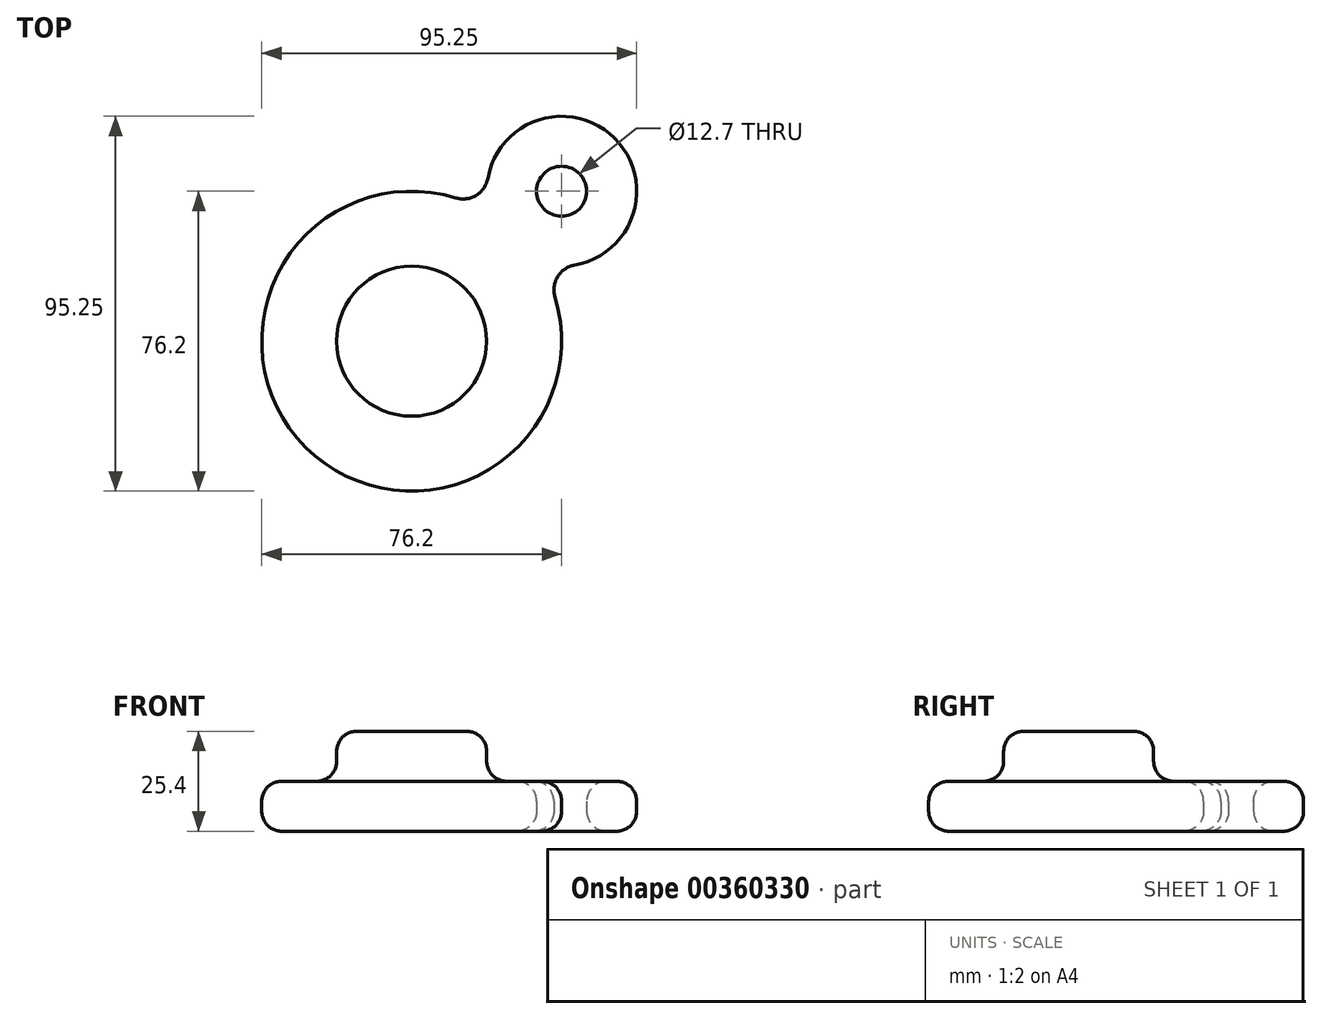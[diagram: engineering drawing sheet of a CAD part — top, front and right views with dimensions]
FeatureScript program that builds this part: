
annotation { "Feature Type Name" : "Feature", "Feature Type Description" : "" }
export const myFeature = defineFeature(function(context is Context, id is Id, definition is map)
    precondition{}
    {
        {
            var Q0;
            Q0=qCreatedBy(makeId("Top.planeOp"),FACE);
            var sketch = newSketch(context, id + "F0", { "sketchPlane" : qUnion([Q0])});
            skArc(sketch, "E0", {"start": v(11.21, 36.41) * mm, "mid": v(-26.94, -26.94) * mm, "end": v(36.41, 11.21) * mm});
            skArc(sketch, "E1", {"start": v(41.39, 19.34) * mm, "mid": v(51.57, 51.57) * mm, "end": v(19.34, 41.39) * mm});
            skPoint(sketch, "E2.visualSharp", {"position": v(19.9, 32.5) * mm});
            skArc(sketch, "E2.filletArc", {"start": v(11.21, 36.41) * mm, "mid": v(16.4, 37.07) * mm, "end": v(19.34, 41.39) * mm});
            skPoint(sketch, "E3.visualSharp", {"position": v(32.5, 19.9) * mm});
            skArc(sketch, "E3.filletArc", {"start": v(41.39, 19.34) * mm, "mid": v(37.07, 16.4) * mm, "end": v(36.41, 11.21) * mm});
            skCircle(sketch, "E4", {"center": v(38.1, 38.1) * mm, "radius": 6.35 * mm});
            skSolve(sketch);
        }
        {
            var Q0;
            Q0=qCreatedBy(makeId("Top.planeOp"),FACE);
            var sketch = newSketch(context, id + "F1", { "sketchPlane" : qUnion([Q0])});
            skCircle(sketch, "E5", {"center": v(0, 0) * mm, "radius": 19.05 * mm});
            skSolve(sketch);
        }
        {
            var Q0;
            Q0=makeQuery(id+"F0.imprint","IMPRINT",FACE,{"disambiguationData":[TD([[makeQuery(id+"F0.imprint","IMPRINT",EDGE,{"derivedFrom":sQuery(id+"F0.wireOp",EDGE,"E0")}),1.0]])]});
            extrude(context, id + "F2", {"entities" : qUnion([Q0]), "depth" : 12.7 * mm});
        }
        {
            var Q0;
            Q0=makeQuery(id+"F1.imprint","IMPRINT",FACE,{"disambiguationData":[TD([[makeQuery(id+"F1.imprint","IMPRINT",EDGE,{"derivedFrom":sQuery(id+"F1.wireOp",EDGE,"E5")}),1.0]])]});
            extrude(context, id + "F3", {"entities" : qUnion([Q0]), "operationType" : NewBodyOperationType.ADD, "depth" : 25.4 * mm});
        }
        {
            var Q0;
            Q0=makeQuery(id+"F3.opExtrude","CAP_EDGE",EDGE,{"disambiguationData":[OSD([sQuery(id+"F1.wireOp",EDGE,"E5")])],"isStart":false});
            var Q1;
            Q1=makeQuery(id+"F2.opExtrude","CAP_EDGE",EDGE,{"disambiguationData":[OSD([sQuery(id+"F0.wireOp",EDGE,"E0")])],"isStart":false});
            var Q2;
            Q2=makeQuery(id+"F2.opExtrude","CAP_EDGE",EDGE,{"disambiguationData":[OSD([sQuery(id+"F0.wireOp",EDGE,"E0")])],"isStart":true});
            var Q3;
            Q3=makeQuery(id+"F3.boolean.opBoolean","INTERSECT",EDGE,{"derivedFrom":[makeQuery(id+"F2.opExtrude","CAP_FACE",FACE,{"disambiguationData":[OSD([sQuery(id+"F0.wireOp",EDGE,"E0"),sQuery(id+"F0.wireOp",EDGE,"E1"),sQuery(id+"F0.wireOp",EDGE,"E2.filletArc"),sQuery(id+"F0.wireOp",EDGE,"E3.filletArc"),sQuery(id+"F0.wireOp",EDGE,"E4")])],"isStart":false}),makeQuery(id+"F3.opExtrude","SWEPT_FACE",FACE,{"disambiguationData":[OSD([sQuery(id+"F1.wireOp",EDGE,"E5")])]})]});
            var Q4;
            Q4=makeQuery(id+"F2.opExtrude","CAP_EDGE",EDGE,{"disambiguationData":[OSD([sQuery(id+"F0.wireOp",EDGE,"E4")])],"isStart":false});
            var Q5;
            Q5=makeQuery(id+"F2.opExtrude","CAP_EDGE",EDGE,{"disambiguationData":[OSD([sQuery(id+"F0.wireOp",EDGE,"E4")])],"isStart":true});
            fillet(context, id + "F4", {"entities" : qUnion([Q0, Q1, Q2, Q3, Q4, Q5]), "radius" : 5.08 * mm, "tangentPropagation" : true, "allowEdgeOverflow" : false});
        }
    });
